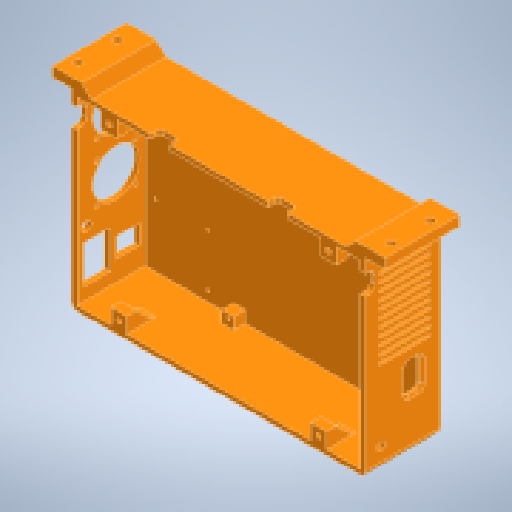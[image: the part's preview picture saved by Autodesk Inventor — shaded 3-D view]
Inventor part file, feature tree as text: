
AUTODESK INVENTOR PART (.ipt)
format: ipt  version: 2024.1 (Build 281209000, 209)  size: 694,784 bytes
history: native  units: in
note: dims shown in document units (in); Inventor stores cm internally (conversion verified against a paired STEP export)
features: extrude x21, sketch x21, fillet x6, chamfer x4
ambient origin geometry x8: Origin, YZ Plane, XZ Plane, XY Plane, X Axis, Y Axis, Z Axis, Center Point
bodies: Solid1 (feature_tree)
feature tree (52):
  extrude  "Extrusion1"  Depth=5.9055in
  extrude  "Extrusion2"  Depth=0.0984in
  extrude  "Extrusion3"  Depth=0.0984in
  extrude  "Extrusion4"  Depth=1.378in TaperAngle=0.0deg
  extrude  "Extrusion5"  Depth=0.2362in
  extrude  "Extrusion6"  Depth=0.2362in
  extrude  "Extrusion7"  Depth=0.2362in
  fillet  "Fillet1"  Radius=0.2362in
  chamfer  "Chamfer1"  Distance=0.2362in
  extrude  "Extrusion8"  Depth=0.1575in
  fillet  "Fillet2"  Radius=0.1575in
  extrude  "Extrusion9"  Depth=0.0709in
  extrude  "Extrusion10"  Depth=0.0787in
  chamfer  "Chamfer2"  [1 undecoded]
  extrude  "Extrusion11"  Depth=0.0709in
  extrude  "Extrusion12"  Depth=0.0787in
  fillet  "Fillet3"  Radius=0.0984in
  fillet  "Fillet4"  Radius=0.0886in
  extrude  "Extrusion13"  Depth=0.315in
  extrude  "Extrusion14"  Depth=0.8858in
  extrude  "Extrusion15"  TaperAngle=0.0deg  [1 undecoded]
  extrude  "Extrusion16"  Depth=0.0591in TaperAngle=45.0deg
  extrude  "Extrusion17"  Depth=0.2756in
  chamfer  "Chamfer3"  Distance=1.811in
  extrude  "Extrusion18"  Depth=4.3307in
  extrude  "Extrusion19"  TaperAngle=0.0deg  [1 undecoded]
  chamfer  "Chamfer4"  Distance=0.0295in
  extrude  "Extrusion20"  Depth=0.9449in
  fillet  "Fillet5"  Radius=0.6299in
  extrude  "Extrusion21"  Depth=0.7874in
  fillet  "Fillet6"  [1 undecoded]
  sketch  "Sketch1"  dims[d0=3.8287in d1=5.9055in]
  sketch  "Sketch2"  dims[d2=1.4961in d3=0.0in d4=0.0984in]
  sketch  "Sketch3"  dims[d5=0.0984in d6=0.0984in]
  sketch  "Sketch4"  dims[d7=0.0984in d8=1.378in d9=0.0in]
  sketch  "Sketch5"  dims[d10=0.2362in d11=0.2362in]
  sketch  "Sketch6"  dims[d12=0.2362in d13=0.2362in]
  sketch  "Sketch7"  dims[d14=0.2362in d15=0.2362in d16=0.2362in]
  sketch  "Sketch8"  dims[d17=0.2362in]
  sketch  "Sketch10"  dims[d18=3.4646in]
  sketch  "Sketch11"  dims[d19=3.4646in d20=0.2362in d21=0.0in]
  sketch  "Sketch12"  dims[d22=0.0709in d23=0.1476in d24=0.1575in]
  sketch  "Sketch13"  dims[d25=0.0in d26=0.0in d27=0.0709in]
  sketch  "Sketch14"  dims[d28=0.0787in d29=0.0787in d30=0.0in d31=0.0in]
  sketch  "Sketch15"  dims[d32=0.0709in d33=0.0709in]
  sketch  "Sketch16"  dims[d34=0.0984in d35=0.0787in d36=0.0984in d37=0.0886in]
  sketch  "Sketch17"  dims[d38=0.0in d39=0.0in d40=0.315in]
  sketch  "Sketch18"  dims[d41=0.5906in d42=0.8858in]
  sketch  "Sketch19"  dims[d43=0.2559in d44=0.0in d45=0.0in]
  sketch  "Sketch20"  dims[d46=0.0787in d47=0.0591in d48=0.0787in d49=45.0deg]
  sketch  "Sketch21"  dims[d50=0.0591in d51=0.2756in]
  sketch  "Sketch22"  dims[d52=0.1969in d53=1.811in d54=4.3307in d56=0.1575in d57=0.3937in d59=0.3937in d61=0.0in d62=0.0in d63=0.0295in d64=0.9449in d66=0.6299in d67=0.7874in d70=0.0in d71=0.0in d72=0.0866in d73=0.0866in d75=0.0866in d76=0.3937in d77=0.3937in d79=0.3937in d80=0.3937in d81=0.3937in d82=0.3937in d83=0.0866in d84=0.3937in d85=0.3937in d86=0.3937in d87=0.0in d88=0.0591in d89=0.0787in d90=45.0deg d91=0.7874in d93=1.1811in d94=0.3937in d96=0.3937in d98=0.7874in d100=1.1811in d101=0.3937in d103=0.3937in d105=0.5197in d106=0.7677in d107=0.8268in d108=0.3543in d109=0.3937in d110=0.0in d111=0.1969in d112=0.3937in d113=0.2756in d114=0.0in d115=0.0in d116=0.1181in d117=0.1181in d118=0.4724in d119=0.3937in d120=0.2362in d121=0.5118in d122=0.3937in d123=0.0in d124=0.1575in d125=0.315in d126=0.3937in d127=0.3937in d128=0.0in d129=0.1969in d130=0.1969in d131=1.378in d132=0.3937in d133=0.0in d134=0.063in d135=0.063in d136=0.063in d137=0.1969in d138=1.2598in d139=1.2598in d140=1.2598in d141=0.1969in d142=1.2598in d143=0.3937in d144=0.0in d145=0.5906in d146=0.5906in d147=1.4961in d148=1.4961in d149=0.1969in d150=0.1969in d151=0.1969in d152=0.0in d153=0.1969in d154=0.0787in d155=45.0deg d156=0.1654in d157=0.1654in d158=0.1654in d159=0.1654in d160=0.315in d161=0.1969in d162=0.3937in d163=0.1969in d164=0.1969in d165=0.315in d166=0.1969in d167=0.3937in d168=0.1969in d169=0.0in d170=0.315in d171=0.4134in d172=0.315in d173=0.4134in d174=0.4134in d175=0.315in d176=0.315in d177=0.4134in d178=0.5906in d179=0.5906in d180=0.7874in d181=0.7874in d182=0.1969in d183=0.0in d184=0.315in d185=0.0787in d186=45.0deg d187=0.1024in d188=0.1024in d189=0.1024in d190=0.1024in d191=0.1575in d192=0.1575in d193=0.1575in d194=0.1575in d195=0.1575in d196=0.1575in d197=0.1575in d198=0.1575in d199=0.1969in d200=0.0in d201=0.1969in d202=0.3937in d203=0.3937in d204=1.5748in d205=1.5748in d206=0.1969in d207=0.0in d208=0.0787in]
note: 4 required parameter values undecoded (feature->parameter linkage not recoverable at this tier; creation-order binding heuristic only, values carry confidence <= 0.55)
